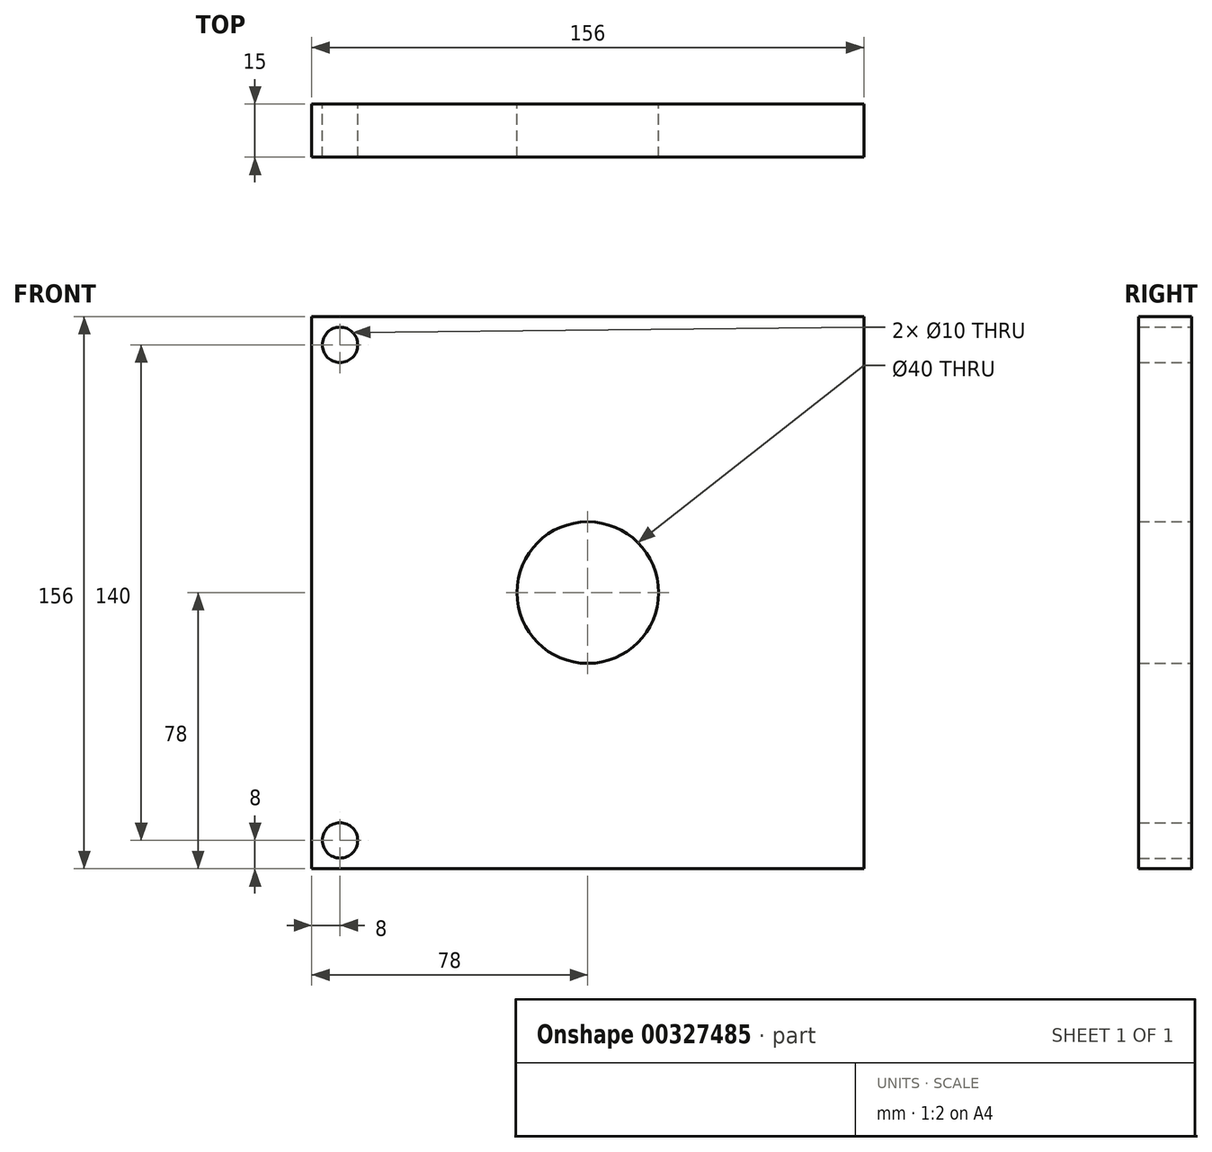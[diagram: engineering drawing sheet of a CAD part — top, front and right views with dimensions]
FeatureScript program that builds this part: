
annotation { "Feature Type Name" : "Feature", "Feature Type Description" : "" }
export const myFeature = defineFeature(function(context is Context, id is Id, definition is map)
    precondition{}
    {
        {
            var Q0;
            Q0=qCreatedBy(makeId("Front.planeOp"),FACE);
            var sketch = newSketch(context, id + "F0", { "sketchPlane" : qUnion([Q0])});
            skLineSegment(sketch, "E0.bottom", {"start": v(-78, -78) * mm, "end": v(78, -78) * mm});
            skLineSegment(sketch, "E0.top", {"start": v(-78, 78) * mm, "end": v(78, 78) * mm});
            skLineSegment(sketch, "E0.left", {"start": v(-78, -78) * mm, "end": v(-78, 78) * mm});
            skLineSegment(sketch, "E0.right", {"start": v(78, -78) * mm, "end": v(78, 78) * mm});
            skPoint(sketch, "E0.middle", {"position": v(0, 0) * mm});
            skLineSegment(sketch, "E1", {"start": v(-78, -78) * mm, "end": v(-73, -78) * mm});
            skLineSegment(sketch, "E2.MirrorCS", {"start": v(-78, 78) * mm, "end": v(-73, 78) * mm});
            skLineSegment(sketch, "E3.MirrorCS", {"start": v(-78, 78) * mm, "end": v(-78, -78) * mm});
            skLineSegment(sketch, "E4.MirrorCS", {"start": v(78, 78) * mm, "end": v(73, 78) * mm});
            skLineSegment(sketch, "E5.MirrorCS", {"start": v(78, -78) * mm, "end": v(73, -78) * mm});
            skLineSegment(sketch, "E6.MirrorCS", {"start": v(78, 78) * mm, "end": v(-78, 78) * mm});
            skLineSegment(sketch, "E7.MirrorCS", {"start": v(78, 78) * mm, "end": v(78, -78) * mm});
            skLineSegment(sketch, "E8.MirrorCS", {"start": v(78, -78) * mm, "end": v(-78, -78) * mm});
            skCircle(sketch, "E9", {"center": v(0, 0) * mm, "radius": 20 * mm});
            skCircle(sketch, "E10", {"center": v(-70, 70) * mm, "radius": 5 * mm});
            skLineSegment(sketch, "E11", {"start": v(-70, 70) * mm, "end": v(70, 70) * mm, "construction": true});
            skLineSegment(sketch, "E12", {"start": v(70, 70) * mm, "end": v(70, -70) * mm, "construction": true});
            skLineSegment(sketch, "E13", {"start": v(70, -70) * mm, "end": v(-70, -70) * mm, "construction": true});
            skLineSegment(sketch, "E14", {"start": v(-70, -70) * mm, "end": v(-70, 70) * mm, "construction": true});
            skCircle(sketch, "E15", {"center": v(-70, -70) * mm, "radius": 5 * mm});
            skSolve(sketch);
        }
        {
            var Q0;
            Q0 = qSketchRegion(id + "F0", true);
            extrude(context, id + "F1", {"entities" : qUnion([Q0]), "depth" : 15 * mm});
        }
    });
